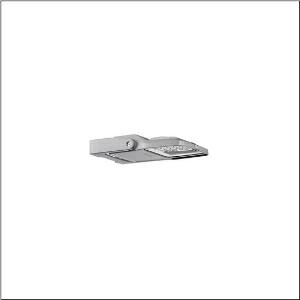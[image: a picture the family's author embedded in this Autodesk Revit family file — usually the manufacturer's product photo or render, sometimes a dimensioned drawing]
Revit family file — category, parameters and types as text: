
# Revit family: floodlight_fl_21_iq_micro___pl64_5xa7762a4e2a_da81
name_source: partatom
category: Lighting Fixtures
units: mm (PartAtom-declared; Revit-internal decimal feet)

## family parameters
Cut with Voids When Loaded = No
Host = Face
Light Source = No
Part Type = Normal
Room Calculation Point = No
Round Connector Dimension = Use Diameter
Shared = No

## types (1)
- --- (1 x LED, 2980 lm, 23.1 W, 4000K)
    Apparent Load = 23 VA
    CIE Flux Codes = 28 80 98 100 100
    Color Rendering = 70
    Color Temperature = 4000K
    Default Elevation = 1800 mm
    Description = Floodlight FL 21 iQ micro, floodlight, primary light control with lens, of PMMA, primary optical cover: protective disc, of toughened safety glass, transparent, light distribution: PL64, light emission: direct distribution, installation type: surface-mounted, LED, High Power LED, rated luminous flux: 2.980lm, luminous efficacy: 129lm/W, light colour: 740, colour temperature: 4000K, control: Auto-Match, Temp-Guard, Night-Set, Smart-Wire, Desk-Remote (wireless, voltage-free reading and setting of iQ features in the workshop via application-optimized NFC function/RFID function), optimised constant luminous flux control (CLO 2.0), Street-Remote, with terminal, 6-pole, mains connection: 220..240V, AC, 50/60Hz, start of lifetime: 23W, end of service life: 24W, reduction: 11W, luminaire housing, of diecast aluminium, powder-coated, Siteco® metallic grey (DB 702S), corrosivity category C5 mid according to DIN EN ISO 12944, sealing non-destructively replaceable, design bracket, of diecast aluminium, powder-coated, Siteco® metallic grey (DB 702S), protection rating (complete): IP66, insulation class (complete): insulation class II (safety insulation), certification: CE, ENEC, VDE, protection symbol: D, impact resistance: IK07, permissible operating ambient temperature: -40..+40°C, permissible operating ambient temperature for outdoor applications: -40..+50°C, standard: DIN EN 12944, LABS conformity tested according to VDMA 24364:2018-05, packaging unit: 1 piece

Light Distribution: PL64
    Height = 65 mm
    Lamp = 1 x LED
    Lamp Light Flux = 2980 lm
    Lamp Power = 23.1 W
    Lamp count = 1
    Length = 312 mm
    Luminous efficacy = 129 lm/W
    Manufacturer = Siteco
    ModVariant = No
    Model = 5XA7762A4E2A
    Mounting Place = Wall
    Mounting Type = Surface mounted
    Number of Poles = 1
    OnlyDefault = Yes
    Power Factor = 1
    Product Name = Floodlight FL 21 iQ micro | PL64
    Product group = floodlight | wall mounted
    ProductGroupID = 2001
    Protection Class = Protection class II
    Protection Degree = IP 66
    RLX_Detail_Level = 1
    RLX_Emergency_Light_Flux = 0 lm
    RLX_Emergency_Type = 0
    RLX_Emergency_Type_DB = No
    RlxData = <blob elided: 97261 chars, md5=8f86767f>
    Socket = socket
    Standby Power = 0 W
    System Light Flux = 2980 lm
    System Power = 23 W
    Type Comments = factory setting: luminous flux: 100 % | dim-lin: 254 | 455 mA
    Type Image = l_1006878.jpg
    URL = http://relux.com
    VarID = @adj_113611
    Voltage = 0 V
    Weight = 0.00 kg
    Width = 230 mm

## geometry (parser evidence)
native form markers: Blend x4, Sweep x13
no freeform markers — native parametric forms only
